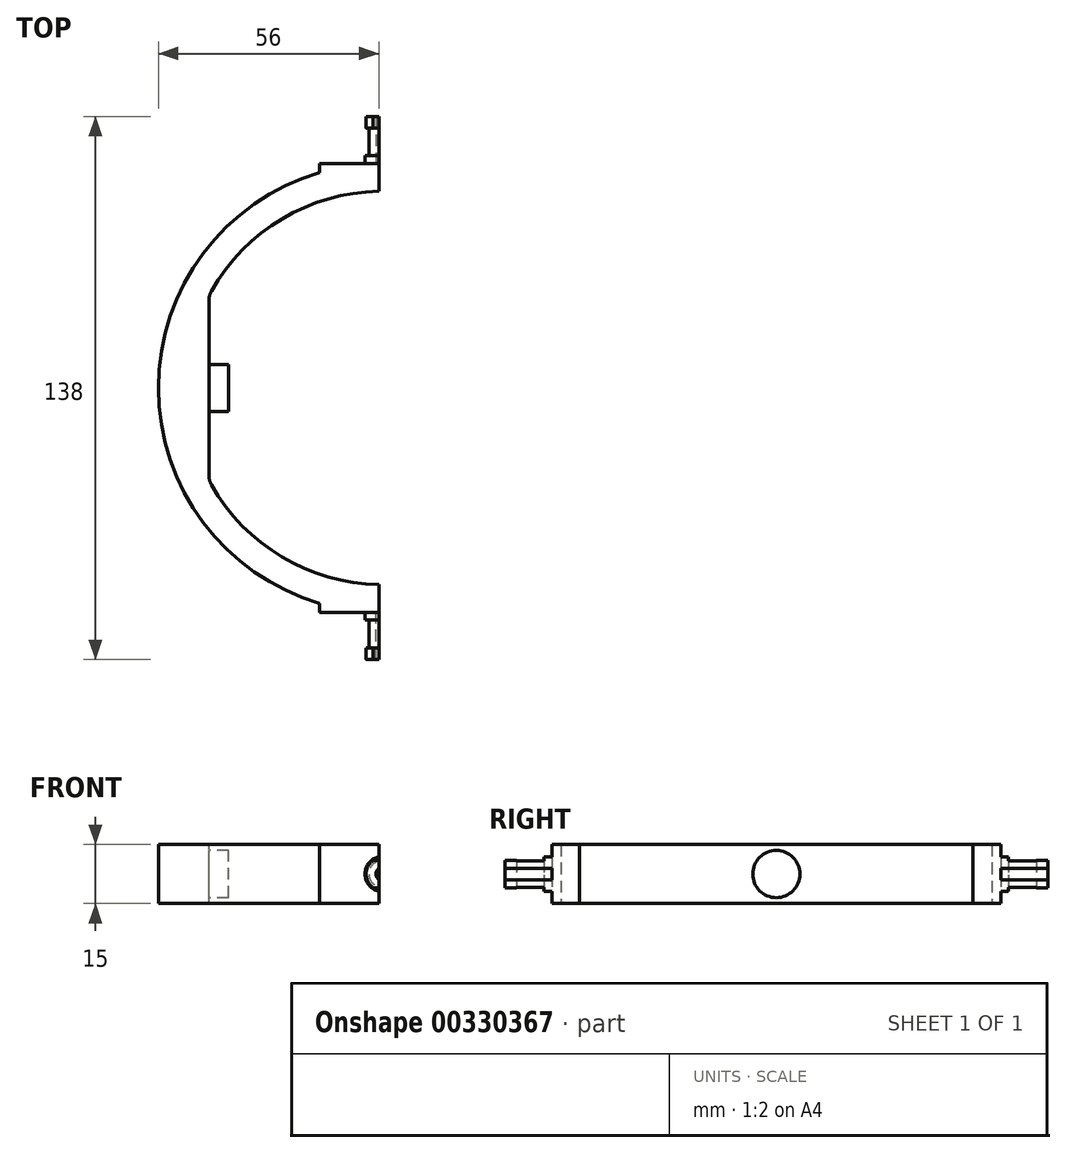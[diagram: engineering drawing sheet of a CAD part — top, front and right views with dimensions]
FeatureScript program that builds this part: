
annotation { "Feature Type Name" : "Feature", "Feature Type Description" : "" }
export const myFeature = defineFeature(function(context is Context, id is Id, definition is map)
    precondition{}
    {
        {
            var Q0;
            Q0=qCreatedBy(makeId("Top.planeOp"),FACE);
            var sketch = newSketch(context, id + "F0", { "sketchPlane" : qUnion([Q0])});
            skArc(sketch, "E0", {"start": v(0, 50) * mm, "mid": v(-25.76, 42.85) * mm, "end": v(-44.16, 23.45) * mm});
            skLineSegment(sketch, "E1", {"start": v(-44.16, 23.45) * mm, "end": v(-44.16, -23.45) * mm});
            skArc(sketch, "E2", {"start": v(-16, 54.7) * mm, "mid": v(-57, 0) * mm, "end": v(-16, -54.7) * mm});
            skLineSegment(sketch, "E3", {"start": v(0, 57) * mm, "end": v(0, 50) * mm});
            skLineSegment(sketch, "E4", {"start": v(0, -50) * mm, "end": v(0, -57) * mm});
            skArc(sketch, "E5.trimOffspring", {"start": v(-44.16, -23.45) * mm, "mid": v(-25.76, -42.85) * mm, "end": v(0, -50) * mm});
            skLineSegment(sketch, "E6", {"start": v(0, -57) * mm, "end": v(-16, -57) * mm});
            skLineSegment(sketch, "E7", {"start": v(-16, -57) * mm, "end": v(-16, -54.7) * mm});
            skLineSegment(sketch, "E8", {"start": v(0, 57) * mm, "end": v(-16, 57) * mm});
            skLineSegment(sketch, "E9", {"start": v(-16, 57) * mm, "end": v(-16, 54.7) * mm});
            skSolve(sketch);
        }
        {
            var Q0;
            Q0=makeQuery(id+"F0.imprint","IMPRINT",FACE,{"disambiguationData":[TD([[makeQuery(id+"F0.imprint","IMPRINT",EDGE,{"derivedFrom":sQuery(id+"F0.wireOp",EDGE,"E0")}),-1.0]])]});
            extrude(context, id + "F1", {"entities" : qUnion([Q0]), "depth" : 15 * mm});
        }
        {
            var Q0;
            Q0=makeQuery(id+"F1.opExtrude","SWEPT_FACE",FACE,{"disambiguationData":[OSD([sQuery(id+"F0.wireOp",EDGE,"E1")])]});
            var sketch = newSketch(context, id + "F2", { "sketchPlane" : qUnion([Q0])});
            skLineSegment(sketch, "E10", {"start": v(-23.45, 15) * mm, "end": v(23.45, 0) * mm, "construction": true});
            skLineSegment(sketch, "E11", {"start": v(-23.45, 0) * mm, "end": v(23.45, 15) * mm, "construction": true});
            skCircle(sketch, "E12", {"center": v(0, 7.5) * mm, "radius": 6 * mm});
            skSolve(sketch);
        }
        {
            var Q0;
            Q0=makeQuery(id+"F2.imprint","IMPRINT",FACE,{"disambiguationData":[TD([[makeQuery(id+"F2.imprint","IMPRINT",EDGE,{"derivedFrom":sQuery(id+"F2.wireOp",EDGE,"E12")}),1.0]])]});
            extrude(context, id + "F3", {"entities" : qUnion([Q0]), "operationType" : NewBodyOperationType.ADD, "depth" : 5 * mm});
        }
        {
            var Q0;
            Q0=makeQuery(id+"F1.opExtrude","SWEPT_EDGE",EDGE,{"disambiguationData":[OSD([sQuery(id+"F0.wireOp",EDGE,"E0"),sQuery(id+"F0.wireOp",EDGE,"E1")])]});
            var Q1;
            Q1=makeQuery(id+"F1.opExtrude","SWEPT_EDGE",EDGE,{"disambiguationData":[OSD([sQuery(id+"F0.wireOp",EDGE,"E1"),sQuery(id+"F0.wireOp",EDGE,"E5.trimOffspring")])]});
            fillet(context, id + "F4", {"entities" : qUnion([Q0, Q1]), "radius" : 5 * mm, "tangentPropagation" : true, "allowEdgeOverflow" : false});
        }
        {
            var Q0;
            Q0=makeQuery(id+"F1.opExtrude","SWEPT_FACE",FACE,{"disambiguationData":[OSD([sQuery(id+"F0.wireOp",EDGE,"E6")])]});
            var sketch = newSketch(context, id + "F5", { "sketchPlane" : qUnion([Q0])});
            skArc(sketch, "E13", {"start": v(0, 12) * mm, "mid": v(-4.5, 7.5) * mm, "end": v(0, 3) * mm});
            skArc(sketch, "E14", {"start": v(0, 9.25) * mm, "mid": v(-1.75, 7.5) * mm, "end": v(0, 5.75) * mm});
            skLineSegment(sketch, "E15", {"start": v(0, 12) * mm, "end": v(0, 9.25) * mm});
            skLineSegment(sketch, "E16", {"start": v(0, 9.25) * mm, "end": v(0, 5.75) * mm});
            skLineSegment(sketch, "E17", {"start": v(0, 5.75) * mm, "end": v(0, 3) * mm});
            skLineSegment(sketch, "E18", {"start": v(0, 5.75) * mm, "end": v(0, 9.25) * mm});
            skSolve(sketch);
        }
        {
            var Q0;
            Q0=makeQuery(id+"F5.imprint","IMPRINT",FACE,{"disambiguationData":[TD([[makeQuery(id+"F5.imprint","IMPRINT",EDGE,{"derivedFrom":sQuery(id+"F5.wireOp",EDGE,"E13")}),1.0]])]});
            extrude(context, id + "F6", {"entities" : qUnion([Q0]), "operationType" : NewBodyOperationType.ADD, "depth" : 2 * mm});
        }
        {
            var Q0;
            Q0=makeQuery(id+"F6.opExtrude","CAP_FACE",FACE,{"disambiguationData":[OSD([sQuery(id+"F5.wireOp",EDGE,"E13"),sQuery(id+"F5.wireOp",EDGE,"E14"),sQuery(id+"F5.wireOp",EDGE,"E15"),sQuery(id+"F5.wireOp",EDGE,"E17")])],"isStart":false});
            var sketch = newSketch(context, id + "F7", { "sketchPlane" : qUnion([Q0])});
            skArc(sketch, "E19", {"start": v(0, 11) * mm, "mid": v(-3.5, 7.5) * mm, "end": v(0, 4) * mm});
            skLineSegment(sketch, "E20", {"start": v(0, 11) * mm, "end": v(0, 9.25) * mm});
            skLineSegment(sketch, "E21", {"start": v(0, 9.25) * mm, "end": v(0, 5.75) * mm});
            skLineSegment(sketch, "E22", {"start": v(0, 5.75) * mm, "end": v(0, 4) * mm});
            skSolve(sketch);
        }
        {
            var Q0;
            Q0=makeQuery(id+"F7.imprint","IMPRINT",FACE,{"disambiguationData":[TD([[makeQuery(id+"F7.imprint","IMPRINT",EDGE,{"derivedFrom":sQuery(id+"F7.wireOp",EDGE,"E19")}),1.0]])]});
            extrude(context, id + "F8", {"entities" : qUnion([Q0]), "operationType" : NewBodyOperationType.ADD, "depth" : 7 * mm});
        }
        {
            var Q0;
            Q0=makeQuery(id+"F8.opExtrude","CAP_FACE",FACE,{"disambiguationData":[OSD([sQuery(id+"F5.wireOp",EDGE,"E14"),sQuery(id+"F7.wireOp",EDGE,"E19"),sQuery(id+"F7.wireOp",EDGE,"E20"),sQuery(id+"F7.wireOp",EDGE,"E22")])],"isStart":false});
            var sketch = newSketch(context, id + "F9", { "sketchPlane" : qUnion([Q0])});
            skArc(sketch, "E23", {"start": v(0, 11.75) * mm, "mid": v(-4.25, 7.5) * mm, "end": v(0, 3.25) * mm});
            skLineSegment(sketch, "E24", {"start": v(0, 3.25) * mm, "end": v(0, 11.75) * mm});
            skSolve(sketch);
        }
        {
            var Q0;
            Q0=qSketchRegion(id+"F9",true);
            extrude(context, id + "F10", {"entities" : qUnion([Q0]), "operationType" : NewBodyOperationType.ADD, "depth" : 3 * mm});
        }
        {
            var Q0;
            {var subQ0=sQuery(id+"F5.wireOp",EDGE,"E14");var subQ1=sQuery(id+"F9.wireOp",EDGE,"E24");Q0=makeQuery(id+"F10.boolean.opBoolean","SPLIT",FACE,{"disambiguationData":[TD([makeQuery(id+"F6.opExtrude","SWEPT_FACE",FACE,{"disambiguationData":[OSD([subQ0])]})])],"derivedFrom":makeQuery(id+"F10.opExtrude","CAP_FACE",FACE,{"disambiguationData":[OSD([sQuery(id+"F9.wireOp",EDGE,"E23"),subQ1])],"isStart":true})});}
            extrude(context, id + "F11", {"entities" : qUnion([Q0]), "operationType" : NewBodyOperationType.REMOVE, "oppositeDirection" : true, "depth" : 25 * mm});
        }
        {
            var Q0;
            Q0=makeQuery(id+"F1.opExtrude","SWEPT_BODY",BODY,{"disambiguationData":[OSD([sQuery(id+"F0.wireOp",EDGE,"E0"),sQuery(id+"F0.wireOp",EDGE,"E1"),sQuery(id+"F0.wireOp",EDGE,"E2"),sQuery(id+"F0.wireOp",EDGE,"E3"),sQuery(id+"F0.wireOp",EDGE,"E4"),sQuery(id+"F0.wireOp",EDGE,"E5.trimOffspring"),sQuery(id+"F0.wireOp",EDGE,"E6"),sQuery(id+"F0.wireOp",EDGE,"E7"),sQuery(id+"F0.wireOp",EDGE,"E8"),sQuery(id+"F0.wireOp",EDGE,"E9")])]});
            var Q1;
            Q1=qCreatedBy(makeId("Front.planeOp"),FACE);
            mirror(context, id + "F12", {"operationType" : NewBodyOperationType.ADD, "entities" : qUnion([Q0]), "mirrorPlane" : qUnion([Q1])});
        }
        {
            var Q0;
            Q0=qCreatedBy(makeId("Right.planeOp"),FACE);
            var sketch = newSketch(context, id + "F13", { "sketchPlane" : qUnion([Q0])});
            skLineSegment(sketch, "E25.bottom", {"start": v(-73.13, 21.61) * mm, "end": v(73.72, 21.61) * mm});
            skLineSegment(sketch, "E25.top", {"start": v(-73.13, -6.51) * mm, "end": v(73.72, -6.51) * mm});
            skLineSegment(sketch, "E25.left", {"start": v(-73.13, 21.61) * mm, "end": v(-73.13, -6.51) * mm});
            skLineSegment(sketch, "E25.right", {"start": v(73.72, 21.61) * mm, "end": v(73.72, -6.51) * mm});
            skSolve(sketch);
        }
        {
            var Q0;
            Q0=makeQuery(id+"F13.imprint","IMPRINT",FACE,{"disambiguationData":[TD([[makeQuery(id+"F13.imprint","IMPRINT",EDGE,{"derivedFrom":sQuery(id+"F13.wireOp",EDGE,"E25.bottom")}),-1.0]])]});
            extrude(context, id + "F14", {"entities" : qUnion([Q0]), "operationType" : NewBodyOperationType.REMOVE, "oppositeDirection" : true, "depth" : 1 * mm});
        }
        {
            var Q0;
            Q0=qCreatedBy(makeId("Top.planeOp"),FACE);
            var sketch = newSketch(context, id + "F15", { "sketchPlane" : qUnion([Q0])});
            skLineSegment(sketch, "E26.bottom", {"start": v(-7.64, -70.53) * mm, "end": v(3.73, -70.53) * mm});
            skLineSegment(sketch, "E26.top", {"start": v(-7.64, -59) * mm, "end": v(3.73, -59) * mm});
            skLineSegment(sketch, "E26.left", {"start": v(-7.64, -70.53) * mm, "end": v(-7.64, -59) * mm});
            skLineSegment(sketch, "E26.right", {"start": v(3.73, -70.53) * mm, "end": v(3.73, -59) * mm});
            skLineSegment(sketch, "E27.bottom", {"start": v(-8.8, 59) * mm, "end": v(4.55, 59) * mm});
            skLineSegment(sketch, "E27.top", {"start": v(-8.8, 72.01) * mm, "end": v(4.55, 72.01) * mm});
            skLineSegment(sketch, "E27.left", {"start": v(-8.8, 59) * mm, "end": v(-8.8, 72.01) * mm});
            skLineSegment(sketch, "E27.right", {"start": v(4.55, 59) * mm, "end": v(4.55, 72.01) * mm});
            skSolve(sketch);
        }
        {
            var Q0;
            Q0=makeQuery(id+"F15.imprint","IMPRINT",FACE,{"disambiguationData":[TD([[makeQuery(id+"F15.imprint","IMPRINT",EDGE,{"derivedFrom":sQuery(id+"F15.wireOp",EDGE,"E26.bottom")}),1.0]])]});
            var Q1;
            Q1=makeQuery(id+"F15.imprint","IMPRINT",FACE,{"disambiguationData":[TD([[makeQuery(id+"F15.imprint","IMPRINT",EDGE,{"derivedFrom":sQuery(id+"F15.wireOp",EDGE,"E27.bottom")}),1.0]])]});
            extrude(context, id + "F16", {"entities" : qUnion([Q0, Q1]), "operationType" : NewBodyOperationType.REMOVE, "depth" : 4 * mm});
        }
        {
            var Q0;
            Q0=makeQuery(id+"F1.opExtrude","CAP_FACE",FACE,{"disambiguationData":[OSD([sQuery(id+"F0.wireOp",EDGE,"E0"),sQuery(id+"F0.wireOp",EDGE,"E1"),sQuery(id+"F0.wireOp",EDGE,"E2"),sQuery(id+"F0.wireOp",EDGE,"E3"),sQuery(id+"F0.wireOp",EDGE,"E4"),sQuery(id+"F0.wireOp",EDGE,"E5.trimOffspring"),sQuery(id+"F0.wireOp",EDGE,"E6"),sQuery(id+"F0.wireOp",EDGE,"E7"),sQuery(id+"F0.wireOp",EDGE,"E8"),sQuery(id+"F0.wireOp",EDGE,"E9")])],"isStart":false});
            var sketch = newSketch(context, id + "F17", { "sketchPlane" : qUnion([Q0])});
            skLineSegment(sketch, "E28.bottom", {"start": v(-14.22, 71.73) * mm, "end": v(5.3, 71.73) * mm});
            skLineSegment(sketch, "E28.top", {"start": v(-14.22, 59) * mm, "end": v(5.3, 59) * mm});
            skLineSegment(sketch, "E28.left", {"start": v(-14.22, 71.73) * mm, "end": v(-14.22, 59) * mm});
            skLineSegment(sketch, "E28.right", {"start": v(5.3, 71.73) * mm, "end": v(5.3, 59) * mm});
            skLineSegment(sketch, "E29.bottom", {"start": v(-12.24, -59) * mm, "end": v(6.71, -59) * mm});
            skLineSegment(sketch, "E29.top", {"start": v(-12.24, -69.75) * mm, "end": v(6.71, -69.75) * mm});
            skLineSegment(sketch, "E29.left", {"start": v(-12.24, -59) * mm, "end": v(-12.24, -69.75) * mm});
            skLineSegment(sketch, "E29.right", {"start": v(6.71, -59) * mm, "end": v(6.71, -69.75) * mm});
            skSolve(sketch);
        }
        {
            var Q0;
            Q0=makeQuery(id+"F17.imprint","IMPRINT",FACE,{"disambiguationData":[TD([[makeQuery(id+"F17.imprint","IMPRINT",EDGE,{"derivedFrom":sQuery(id+"F17.wireOp",EDGE,"E28.bottom")}),-1.0]])]});
            var Q1;
            Q1=makeQuery(id+"F17.imprint","IMPRINT",FACE,{"disambiguationData":[TD([[makeQuery(id+"F17.imprint","IMPRINT",EDGE,{"derivedFrom":sQuery(id+"F17.wireOp",EDGE,"E29.bottom")}),-1.0]])]});
            extrude(context, id + "F18", {"entities" : qUnion([Q0, Q1]), "operationType" : NewBodyOperationType.REMOVE, "oppositeDirection" : true, "depth" : 4 * mm});
        }
    });
